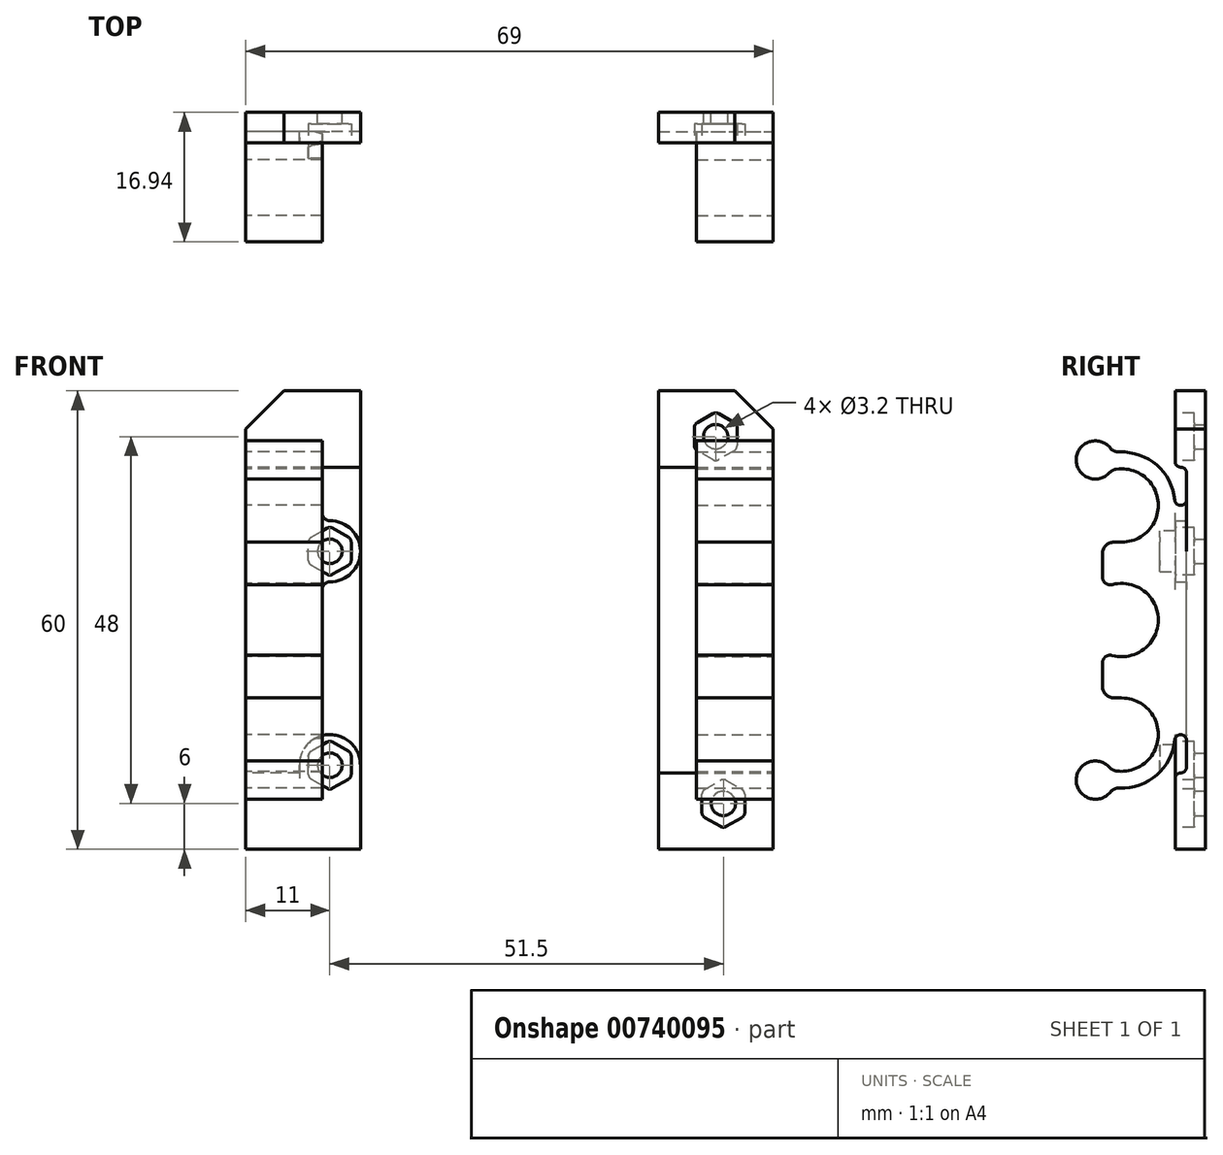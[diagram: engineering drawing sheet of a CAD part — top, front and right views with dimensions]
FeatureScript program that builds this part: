
annotation { "Feature Type Name" : "Feature", "Feature Type Description" : "" }
export const myFeature = defineFeature(function(context is Context, id is Id, definition is map)
    precondition{}
    {
        {
            var Q0;
            Q0=qCreatedBy(makeId("Right.planeOp"),FACE);
            var sketch = newSketch(context, id + "F0", { "sketchPlane" : qUnion([Q0])});
            skLineSegment(sketch, "E0.0", {"start": v(11, -45) * mm, "end": v(11, 15) * mm});
            skLineSegment(sketch, "E1.0", {"start": v(8.5, -34.25) * mm, "end": v(8.5, 4.25) * mm});
            skLineSegment(sketch, "E2.0", {"start": v(7, 5.75) * mm, "end": v(7, 15) * mm});
            skLineSegment(sketch, "E3.0", {"start": v(0, -37) * mm, "end": v(0, 7) * mm, "construction": true});
            skLineSegment(sketch, "E4", {"start": v(11, -15) * mm, "end": v(0, -15) * mm, "construction": true});
            skArc(sketch, "E5", {"start": v(0, -4.8) * mm, "mid": v(4.79, 0.35) * mm, "end": v(-0.7, 4.75) * mm});
            skCircle(sketch, "E6", {"center": v(0, 0) * mm, "radius": 4.38 * mm, "construction": true});
            skArc(sketch, "E7", {"start": v(6.97, 0.7) * mm, "mid": v(4.6, 5.28) * mm, "end": v(-0.29, 7) * mm});
            skLineSegment(sketch, "E8", {"start": v(0, 0) * mm, "end": v(-4.69, 8.12) * mm, "construction": true});
            skArc(sketch, "E9", {"start": v(-1.5, 7.54) * mm, "mid": v(-5.94, 6.02) * mm, "end": v(-1.59, 4.27) * mm});
            skLineSegment(sketch, "E10.0", {"start": v(-2.5, -23.7) * mm, "end": v(-2.5, -20.6) * mm});
            skLineSegment(sketch, "E11.0", {"start": v(11, 15) * mm, "end": v(7, 15) * mm});
            skLineSegment(sketch, "E12.0", {"start": v(7.75, 5) * mm, "end": v(7.75, 5) * mm});
            skLineSegment(sketch, "E13", {"start": v(0, -4.8) * mm, "end": v(-1, -4.8) * mm});
            skArc(sketch, "E14.filletArc", {"start": v(-0.7, 4.75) * mm, "mid": v(-1.18, 4.59) * mm, "end": v(-1.59, 4.27) * mm});
            skArc(sketch, "E15.filletArc", {"start": v(-1.5, 7.54) * mm, "mid": v(-0.96, 7.12) * mm, "end": v(-0.29, 7) * mm});
            skArc(sketch, "E16.filletArc", {"start": v(-1, -4.8) * mm, "mid": v(-2.06, -5.24) * mm, "end": v(-2.5, -6.3) * mm});
            skArc(sketch, "E17.filletArc", {"start": v(8.5, 4.25) * mm, "mid": v(8.28, 4.78) * mm, "end": v(7.75, 5) * mm});
            skArc(sketch, "E18.filletArc", {"start": v(7, 5.75) * mm, "mid": v(7.22, 5.22) * mm, "end": v(7.75, 5) * mm});
            skPoint(sketch, "E19", {"position": v(0, -15) * mm});
            skArc(sketch, "E20.MirrorCS", {"start": v(8.5, -34.25) * mm, "mid": v(8.28, -34.78) * mm, "end": v(7.75, -35) * mm});
            skArc(sketch, "E21.MirrorCS", {"start": v(7, -35.75) * mm, "mid": v(7.22, -35.22) * mm, "end": v(7.75, -35) * mm});
            skArc(sketch, "E22.MirrorCS", {"start": v(-1.5, -37.54) * mm, "mid": v(-0.96, -37.12) * mm, "end": v(-0.29, -37) * mm});
            skArc(sketch, "E23.MirrorCS", {"start": v(-1, -25.2) * mm, "mid": v(-2.06, -24.76) * mm, "end": v(-2.5, -23.7) * mm});
            skLineSegment(sketch, "E24.MirrorCS", {"start": v(0, -25.2) * mm, "end": v(-1, -25.2) * mm});
            skArc(sketch, "E25.MirrorCS", {"start": v(-0.7, -34.75) * mm, "mid": v(-1.18, -34.59) * mm, "end": v(-1.59, -34.27) * mm});
            skLineSegment(sketch, "E26.MirrorCS", {"start": v(7, -35.75) * mm, "end": v(7, -45) * mm});
            skCircle(sketch, "E27.MirrorC", {"center": v(0, -30) * mm, "radius": 4.38 * mm, "construction": true});
            skArc(sketch, "E28.MirrorCS", {"start": v(0, -25.2) * mm, "mid": v(4.79, -30.35) * mm, "end": v(-0.7, -34.75) * mm});
            skArc(sketch, "E29.MirrorCS", {"start": v(-1.5, -37.54) * mm, "mid": v(-5.94, -36.02) * mm, "end": v(-1.59, -34.27) * mm});
            skLineSegment(sketch, "E30.MirrorCS", {"start": v(11, -45) * mm, "end": v(7, -45) * mm});
            skLineSegment(sketch, "E31.MirrorCS", {"start": v(7.75, -35) * mm, "end": v(7.75, -35) * mm});
            skLineSegment(sketch, "E32.MirrorCS", {"start": v(0, -30) * mm, "end": v(-4.69, -38.12) * mm, "construction": true});
            skPoint(sketch, "E33.0", {"position": v(11, -41.5) * mm});
            skLineSegment(sketch, "E34", {"start": v(0, 0) * mm, "end": v(8.5, 0) * mm, "construction": true});
            skArc(sketch, "E35", {"start": v(6.97, 0.7) * mm, "mid": v(7.77, 0) * mm, "end": v(8.5, 0.77) * mm});
            skArc(sketch, "E36.MirrorCS", {"start": v(6.97, -30.7) * mm, "mid": v(7.77, -30) * mm, "end": v(8.5, -30.77) * mm});
            skArc(sketch, "E37.MirrorCS", {"start": v(6.97, -30.7) * mm, "mid": v(4.6, -35.28) * mm, "end": v(-0.29, -37) * mm});
            skArc(sketch, "E38", {"start": v(-1.24, -19.64) * mm, "mid": v(4.8, -15) * mm, "end": v(-1.24, -10.36) * mm});
            skLineSegment(sketch, "E39.trimOffspring", {"start": v(-2.5, -9.4) * mm, "end": v(-2.5, -6.3) * mm});
            skArc(sketch, "E40.filletArc", {"start": v(-2.5, -9.4) * mm, "mid": v(-2.1, -10.2) * mm, "end": v(-1.24, -10.36) * mm});
            skArc(sketch, "E41.filletArc", {"start": v(-1.24, -19.64) * mm, "mid": v(-2.1, -19.8) * mm, "end": v(-2.5, -20.6) * mm});
            skSolve(sketch);
        }
        {
            var Q0;
            Q0=makeQuery(id+"F0.imprint","IMPRINT",FACE,{"disambiguationData":[TD([[makeQuery(id+"F0.imprint","IMPRINT",EDGE,{"derivedFrom":sQuery(id+"F0.wireOp",EDGE,"E0.0")}),1.0]])]});
            extrude(context, id + "F1", {"entities" : qUnion([Q0]), "depth" : 15 * mm, "offsetDistance" : 25 * mm});
        }
        {
            var Q0;
            Q0=makeQuery(id+"F0.imprint","IMPRINT",FACE,{"disambiguationData":[TD([[makeQuery(id+"F0.imprint","IMPRINT",EDGE,{"derivedFrom":sQuery(id+"F0.wireOp",EDGE,"E5")}),-1.0]])]});
            extrude(context, id + "F2", {"entities" : qUnion([Q0]), "operationType" : NewBodyOperationType.ADD, "depth" : 10 * mm, "offsetDistance" : 25 * mm});
        }
        {
            var Q0;
            Q0=makeQuery(id+"F1.opExtrude","CAP_EDGE",EDGE,{"disambiguationData":[OSD([sQuery(id+"F0.wireOp",EDGE,"E11.0")])],"isStart":true});
            chamfer(context, id + "F3", {"entities" : qUnion([Q0]), "width" : 5 * mm, "tangentPropagation" : true});
        }
        {
            var Q0;
            Q0=makeQuery(id+"F1.opExtrude","SWEPT_BODY",BODY,{"disambiguationData":[OSD([sQuery(id+"F0.wireOp",EDGE,"E0.0"),sQuery(id+"F0.wireOp",EDGE,"E1.0"),sQuery(id+"F0.wireOp",EDGE,"E2.0"),sQuery(id+"F0.wireOp",EDGE,"E11.0"),sQuery(id+"F0.wireOp",EDGE,"E17.filletArc"),sQuery(id+"F0.wireOp",EDGE,"E18.filletArc"),sQuery(id+"F0.wireOp",EDGE,"E20.MirrorCS"),sQuery(id+"F0.wireOp",EDGE,"E21.MirrorCS"),sQuery(id+"F0.wireOp",EDGE,"E26.MirrorCS"),sQuery(id+"F0.wireOp",EDGE,"E30.MirrorCS")])]});
            var Q1;
            Q1=qCreatedBy(makeId("Right.planeOp"),FACE);
            mirror(context, id + "F4", {"entities" : qUnion([Q0]), "mirrorPlane" : qUnion([Q1])});
        }
        {
            var Q0;
            Q0=makeQuery(id+"F4.opPattern","COPY",BODY,{"derivedFrom":makeQuery(id+"F1.opExtrude","SWEPT_BODY",BODY,{"disambiguationData":[OSD([sQuery(id+"F0.wireOp",EDGE,"E0.0"),sQuery(id+"F0.wireOp",EDGE,"E1.0"),sQuery(id+"F0.wireOp",EDGE,"E2.0"),sQuery(id+"F0.wireOp",EDGE,"E11.0"),sQuery(id+"F0.wireOp",EDGE,"E17.filletArc"),sQuery(id+"F0.wireOp",EDGE,"E18.filletArc"),sQuery(id+"F0.wireOp",EDGE,"E20.MirrorCS"),sQuery(id+"F0.wireOp",EDGE,"E21.MirrorCS"),sQuery(id+"F0.wireOp",EDGE,"E26.MirrorCS"),sQuery(id+"F0.wireOp",EDGE,"E30.MirrorCS")])]}),"instanceName":"1"});
            transform(context, id + "F5", {"entities" : qUnion([Q0]), "transformType" : TransformType.TRANSLATION_3D, "dx" : 69 * mm, "dy" : 0 * mm, "dz" : 0 * mm, "makeCopy" : false});
        }
        {
            var Q0;
            Q0=makeQuery(id+"F1.opExtrude","SWEPT_FACE",FACE,{"disambiguationData":[OSD([sQuery(id+"F0.wireOp",EDGE,"E0.0")])]});
            var sketch = newSketch(context, id + "F6", { "sketchPlane" : qUnion([Q0])});
            skCircle(sketch, "E42", {"center": v(-11, -6) * mm, "radius": 1.6 * mm});
            skCircle(sketch, "E43", {"center": v(-11, -34) * mm, "radius": 1.6 * mm});
            skCircle(sketch, "E44", {"center": v(-61.5, 9) * mm, "radius": 1.6 * mm});
            skCircle(sketch, "E45", {"center": v(-62.5, -39) * mm, "radius": 1.6 * mm});
            skLineSegment(sketch, "E46.0", {"start": v(0, -45) * mm, "end": v(0, 10) * mm, "construction": true});
            skLineSegment(sketch, "E46.1", {"start": v(0, 10) * mm, "end": v(-5, 15) * mm, "construction": true});
            skLineSegment(sketch, "E46.2", {"start": v(-15, 15) * mm, "end": v(-5, 15) * mm, "construction": true});
            skLineSegment(sketch, "E46.3", {"start": v(-15, -45) * mm, "end": v(-15, 15) * mm, "construction": true});
            skLineSegment(sketch, "E46.4", {"start": v(-15, -45) * mm, "end": v(0, -45) * mm, "construction": true});
            skLineSegment(sketch, "E46.5", {"start": v(-54, 15) * mm, "end": v(-64, 15) * mm, "construction": true});
            skLineSegment(sketch, "E46.6", {"start": v(-69, 10) * mm, "end": v(-64, 15) * mm, "construction": true});
            skLineSegment(sketch, "E46.7", {"start": v(-69, -45) * mm, "end": v(-69, 10) * mm, "construction": true});
            skLineSegment(sketch, "E46.8", {"start": v(-54, -45) * mm, "end": v(-69, -45) * mm, "construction": true});
            skLineSegment(sketch, "E46.9", {"start": v(-54, -45) * mm, "end": v(-54, 15) * mm, "construction": true});
            skLineSegment(sketch, "E47", {"start": v(-11, -6) * mm, "end": v(-11, -34) * mm, "construction": true});
            skArc(sketch, "E48", {"start": v(-11, -2) * mm, "mid": v(-15, -6) * mm, "end": v(-11, -10) * mm});
            skArc(sketch, "E49", {"start": v(-7, -34) * mm, "mid": v(-11, -30) * mm, "end": v(-15, -34) * mm});
            skLineSegment(sketch, "E50.0", {"start": v(-15, -35.75) * mm, "end": v(-7, -35.75) * mm});
            skLineSegment(sketch, "E50.1", {"start": v(-10, -11) * mm, "end": v(-10, -1) * mm});
            skArc(sketch, "E51.filletArc", {"start": v(-10, -11) * mm, "mid": v(-10.3, -10.3) * mm, "end": v(-11, -10) * mm});
            skArc(sketch, "E52.filletArc", {"start": v(-11, -2) * mm, "mid": v(-10.3, -1.7) * mm, "end": v(-10, -1) * mm});
            skLineSegment(sketch, "E53", {"start": v(-7, -34) * mm, "end": v(-7, -35.75) * mm});
            skLineSegment(sketch, "E54", {"start": v(-15, -34) * mm, "end": v(-15, -35.75) * mm});
            skPoint(sketch, "E55.orphan", {"position": v(0, -35.75) * mm});
            skSolve(sketch);
        }
        {
            var Q0;
            {var subQ0=sQuery(id+"F6.wireOp",EDGE,"E51.filletArc");Q0=makeQuery(id+"F6.imprint","IMPRINT",FACE,{"disambiguationData":[TD([[makeQuery(id+"F6.imprint","IMPRINT",EDGE,{"derivedFrom":subQ0}),-1.0]])]});}
            var Q1;
            Q1=makeQuery(id+"F6.imprint","IMPRINT",FACE,{"disambiguationData":[TD([[makeQuery(id+"F6.imprint","IMPRINT",EDGE,{"derivedFrom":sQuery(id+"F6.wireOp",EDGE,"E43")}),-1.0]])]});
            extrude(context, id + "F7", {"entities" : qUnion([Q0, Q1]), "operationType" : NewBodyOperationType.ADD, "oppositeDirection" : true, "depth" : 4 * mm, "offsetDistance" : 25 * mm});
        }
        {
            var Q0;
            {var subQ0=sQuery(id+"F6.wireOp",EDGE,"E50.1");var subQ1=sQuery(id+"F6.wireOp",EDGE,"E42");var subQ2=makeQuery(id+"F6.imprint","INTERSECT",VERTEX,{"disambiguationData":[OD(0.0)],"derivedFrom":[subQ1,subQ0]});Q0=makeQuery(id+"F6.imprint","IMPRINT",FACE,{"disambiguationData":[TD([[makeQuery(id+"F6.imprint","IMPRINT",EDGE,{"disambiguationData":[TD([[subQ2,1.0]])],"derivedFrom":subQ1}),1.0]])]});}
            var Q1;
            {var subQ0=sQuery(id+"F6.wireOp",EDGE,"E50.1");var subQ1=sQuery(id+"F6.wireOp",EDGE,"E42");var subQ2=makeQuery(id+"F6.imprint","INTERSECT",VERTEX,{"disambiguationData":[OD(0.0)],"derivedFrom":[subQ1,subQ0]});Q1=makeQuery(id+"F6.imprint","IMPRINT",FACE,{"disambiguationData":[TD([[makeQuery(id+"F6.imprint","IMPRINT",EDGE,{"disambiguationData":[TD([[subQ2,-1.0]])],"derivedFrom":subQ1}),1.0]])]});}
            extrude(context, id + "F8", {"entities" : qUnion([Q0, Q1]), "operationType" : NewBodyOperationType.REMOVE, "oppositeDirection" : true, "depth" : 6 * mm, "offsetDistance" : 25 * mm});
        }
        {
            var Q0;
            Q0=makeQuery(id+"F6.imprint","IMPRINT",FACE,{"disambiguationData":[TD([[makeQuery(id+"F6.imprint","IMPRINT",EDGE,{"derivedFrom":sQuery(id+"F6.wireOp",EDGE,"E43")}),1.0]])]});
            var Q1;
            Q1=makeQuery(id+"F6.imprint","IMPRINT",FACE,{"disambiguationData":[TD([[makeQuery(id+"F6.imprint","IMPRINT",EDGE,{"derivedFrom":sQuery(id+"F6.wireOp",EDGE,"E44")}),1.0]])]});
            var Q2;
            Q2=makeQuery(id+"F6.imprint","IMPRINT",FACE,{"disambiguationData":[TD([[makeQuery(id+"F6.imprint","IMPRINT",EDGE,{"derivedFrom":sQuery(id+"F6.wireOp",EDGE,"E45")}),1.0]])]});
            extrude(context, id + "F9", {"entities" : qUnion([Q0, Q1, Q2]), "operationType" : NewBodyOperationType.REMOVE, "oppositeDirection" : true, "depth" : 4 * mm, "offsetDistance" : 25 * mm});
        }
        {
            var Q0;
            Q0=makeQuery(id+"F1.opExtrude","SWEPT_FACE",FACE,{"disambiguationData":[OSD([sQuery(id+"F0.wireOp",EDGE,"E2.0")])]});
            var sketch = newSketch(context, id + "F10", { "sketchPlane" : qUnion([Q0])});
            skCircle(sketch, "E56.cCircle", {"center": v(11, -6) * mm, "radius": 2.8 * mm, "construction": true});
            skLineSegment(sketch, "E56.0", {"start": v(13.8, -4.82) * mm, "end": v(13.8, -7.18) * mm});
            skLineSegment(sketch, "E56.1", {"start": v(13.43, -7.83) * mm, "end": v(11.38, -9.02) * mm});
            skLineSegment(sketch, "E56.2", {"start": v(10.62, -9.02) * mm, "end": v(8.58, -7.83) * mm});
            skLineSegment(sketch, "E56.3", {"start": v(8.2, -7.18) * mm, "end": v(8.2, -4.82) * mm});
            skLineSegment(sketch, "E56.4", {"start": v(8.57, -4.17) * mm, "end": v(10.62, -2.98) * mm});
            skLineSegment(sketch, "E56.5", {"start": v(11.38, -2.98) * mm, "end": v(13.43, -4.17) * mm});
            skPoint(sketch, "E56.0.midPoint", {"position": v(13.8, -6) * mm});
            skCircle(sketch, "E57.cCircle", {"center": v(11, -34) * mm, "radius": 2.8 * mm, "construction": true});
            skLineSegment(sketch, "E57.0", {"start": v(13.8, -32.82) * mm, "end": v(13.8, -35.18) * mm});
            skLineSegment(sketch, "E57.1", {"start": v(13.42, -35.83) * mm, "end": v(11.37, -37.02) * mm});
            skLineSegment(sketch, "E57.2", {"start": v(10.62, -37.02) * mm, "end": v(8.57, -35.83) * mm});
            skLineSegment(sketch, "E57.3", {"start": v(8.2, -35.18) * mm, "end": v(8.2, -32.82) * mm});
            skLineSegment(sketch, "E57.4", {"start": v(8.57, -32.17) * mm, "end": v(10.62, -30.98) * mm});
            skLineSegment(sketch, "E57.5", {"start": v(11.37, -30.98) * mm, "end": v(13.43, -32.17) * mm});
            skPoint(sketch, "E57.0.midPoint", {"position": v(13.8, -34) * mm});
            skCircle(sketch, "E58.cCircle", {"center": v(61.5, 9) * mm, "radius": 2.8 * mm, "construction": true});
            skLineSegment(sketch, "E58.0", {"start": v(64.3, 10.18) * mm, "end": v(64.3, 7.82) * mm});
            skLineSegment(sketch, "E58.1", {"start": v(63.92, 7.17) * mm, "end": v(61.88, 5.98) * mm});
            skLineSegment(sketch, "E58.2", {"start": v(61.12, 5.98) * mm, "end": v(59.08, 7.17) * mm});
            skLineSegment(sketch, "E58.3", {"start": v(58.7, 7.82) * mm, "end": v(58.7, 10.18) * mm});
            skLineSegment(sketch, "E58.4", {"start": v(59.08, 10.83) * mm, "end": v(61.13, 12.02) * mm});
            skLineSegment(sketch, "E58.5", {"start": v(61.88, 12.02) * mm, "end": v(63.92, 10.83) * mm});
            skPoint(sketch, "E58.0.midPoint", {"position": v(64.3, 9) * mm});
            skCircle(sketch, "E59.cCircle", {"center": v(62.5, -39) * mm, "radius": 2.8 * mm, "construction": true});
            skLineSegment(sketch, "E59.0", {"start": v(65.3, -37.82) * mm, "end": v(65.3, -40.18) * mm});
            skLineSegment(sketch, "E59.1", {"start": v(64.92, -40.83) * mm, "end": v(62.88, -42.02) * mm});
            skLineSegment(sketch, "E59.2", {"start": v(62.13, -42.02) * mm, "end": v(60.07, -40.83) * mm});
            skLineSegment(sketch, "E59.3", {"start": v(59.7, -40.18) * mm, "end": v(59.7, -37.82) * mm});
            skLineSegment(sketch, "E59.4", {"start": v(60.07, -37.17) * mm, "end": v(62.12, -35.98) * mm});
            skLineSegment(sketch, "E59.5", {"start": v(62.88, -35.98) * mm, "end": v(64.92, -37.17) * mm});
            skPoint(sketch, "E59.0.midPoint", {"position": v(65.3, -39) * mm});
            skPoint(sketch, "E60.visualSharp", {"position": v(13.8, -4.38) * mm});
            skArc(sketch, "E60.filletArc", {"start": v(13.8, -4.82) * mm, "mid": v(13.7, -4.44) * mm, "end": v(13.43, -4.17) * mm});
            skPoint(sketch, "E61.visualSharp", {"position": v(11, -2.77) * mm});
            skArc(sketch, "E61.filletArc", {"start": v(11.38, -2.98) * mm, "mid": v(11, -2.88) * mm, "end": v(10.62, -2.98) * mm});
            skPoint(sketch, "E62.visualSharp", {"position": v(8.2, -4.38) * mm});
            skArc(sketch, "E62.filletArc", {"start": v(8.57, -4.17) * mm, "mid": v(8.3, -4.44) * mm, "end": v(8.2, -4.82) * mm});
            skPoint(sketch, "E63.visualSharp", {"position": v(8.2, -7.62) * mm});
            skArc(sketch, "E63.filletArc", {"start": v(8.2, -7.18) * mm, "mid": v(8.3, -7.56) * mm, "end": v(8.58, -7.83) * mm});
            skPoint(sketch, "E64.visualSharp", {"position": v(11, -9.23) * mm});
            skArc(sketch, "E64.filletArc", {"start": v(10.62, -9.02) * mm, "mid": v(11, -9.12) * mm, "end": v(11.38, -9.02) * mm});
            skPoint(sketch, "E65.visualSharp", {"position": v(13.8, -7.62) * mm});
            skArc(sketch, "E65.filletArc", {"start": v(13.43, -7.83) * mm, "mid": v(13.7, -7.56) * mm, "end": v(13.8, -7.18) * mm});
            skPoint(sketch, "E66.visualSharp", {"position": v(13.8, -32.38) * mm});
            skArc(sketch, "E66.filletArc", {"start": v(13.8, -32.82) * mm, "mid": v(13.7, -32.44) * mm, "end": v(13.42, -32.17) * mm});
            skPoint(sketch, "E67.visualSharp", {"position": v(11, -30.77) * mm});
            skArc(sketch, "E67.filletArc", {"start": v(11.37, -30.98) * mm, "mid": v(11, -30.88) * mm, "end": v(10.62, -30.98) * mm});
            skPoint(sketch, "E68.visualSharp", {"position": v(8.2, -32.38) * mm});
            skArc(sketch, "E68.filletArc", {"start": v(8.57, -32.17) * mm, "mid": v(8.3, -32.44) * mm, "end": v(8.2, -32.82) * mm});
            skPoint(sketch, "E69.visualSharp", {"position": v(8.2, -35.62) * mm});
            skArc(sketch, "E69.filletArc", {"start": v(8.2, -35.18) * mm, "mid": v(8.3, -35.56) * mm, "end": v(8.57, -35.83) * mm});
            skPoint(sketch, "E70.visualSharp", {"position": v(11, -37.23) * mm});
            skArc(sketch, "E70.filletArc", {"start": v(10.62, -37.02) * mm, "mid": v(11, -37.12) * mm, "end": v(11.38, -37.02) * mm});
            skPoint(sketch, "E71.visualSharp", {"position": v(13.8, -35.62) * mm});
            skArc(sketch, "E71.filletArc", {"start": v(13.42, -35.83) * mm, "mid": v(13.7, -35.56) * mm, "end": v(13.8, -35.18) * mm});
            skPoint(sketch, "E72.visualSharp", {"position": v(64.3, 10.62) * mm});
            skArc(sketch, "E72.filletArc", {"start": v(64.3, 10.18) * mm, "mid": v(64.2, 10.56) * mm, "end": v(63.92, 10.83) * mm});
            skPoint(sketch, "E73.visualSharp", {"position": v(61.5, 12.23) * mm});
            skArc(sketch, "E73.filletArc", {"start": v(61.88, 12.02) * mm, "mid": v(61.5, 12.12) * mm, "end": v(61.12, 12.02) * mm});
            skPoint(sketch, "E74.visualSharp", {"position": v(58.7, 10.62) * mm});
            skArc(sketch, "E74.filletArc", {"start": v(59.08, 10.83) * mm, "mid": v(58.8, 10.56) * mm, "end": v(58.7, 10.18) * mm});
            skPoint(sketch, "E75.visualSharp", {"position": v(58.7, 7.38) * mm});
            skArc(sketch, "E75.filletArc", {"start": v(58.7, 7.82) * mm, "mid": v(58.8, 7.44) * mm, "end": v(59.08, 7.17) * mm});
            skPoint(sketch, "E76.visualSharp", {"position": v(61.5, 5.77) * mm});
            skArc(sketch, "E76.filletArc", {"start": v(61.12, 5.98) * mm, "mid": v(61.5, 5.88) * mm, "end": v(61.88, 5.98) * mm});
            skPoint(sketch, "E77.visualSharp", {"position": v(64.3, 7.38) * mm});
            skArc(sketch, "E77.filletArc", {"start": v(63.92, 7.17) * mm, "mid": v(64.2, 7.44) * mm, "end": v(64.3, 7.82) * mm});
            skPoint(sketch, "E78.visualSharp", {"position": v(65.3, -37.38) * mm});
            skArc(sketch, "E78.filletArc", {"start": v(65.3, -37.82) * mm, "mid": v(65.2, -37.44) * mm, "end": v(64.92, -37.17) * mm});
            skPoint(sketch, "E79.visualSharp", {"position": v(62.5, -35.77) * mm});
            skArc(sketch, "E79.filletArc", {"start": v(62.88, -35.98) * mm, "mid": v(62.5, -35.88) * mm, "end": v(62.13, -35.98) * mm});
            skPoint(sketch, "E80.visualSharp", {"position": v(59.7, -37.38) * mm});
            skArc(sketch, "E80.filletArc", {"start": v(60.07, -37.17) * mm, "mid": v(59.8, -37.44) * mm, "end": v(59.7, -37.82) * mm});
            skPoint(sketch, "E81.visualSharp", {"position": v(59.7, -40.62) * mm});
            skArc(sketch, "E81.filletArc", {"start": v(59.7, -40.18) * mm, "mid": v(59.8, -40.56) * mm, "end": v(60.07, -40.83) * mm});
            skPoint(sketch, "E82.visualSharp", {"position": v(62.5, -42.23) * mm});
            skArc(sketch, "E82.filletArc", {"start": v(62.13, -42.02) * mm, "mid": v(62.5, -42.12) * mm, "end": v(62.88, -42.02) * mm});
            skPoint(sketch, "E83.visualSharp", {"position": v(65.3, -40.62) * mm});
            skArc(sketch, "E83.filletArc", {"start": v(64.92, -40.83) * mm, "mid": v(65.2, -40.56) * mm, "end": v(65.3, -40.18) * mm});
            skSolve(sketch);
        }
        {
            var Q0;
            Q0 = qSketchRegion(id + "F10", true);
            extrude(context, id + "F11", {"entities" : qUnion([Q0]), "operationType" : NewBodyOperationType.REMOVE, "oppositeDirection" : true, "depth" : 2.5 * mm, "offsetDistance" : 25 * mm});
        }
        {
            var Q0;
            Q0=makeQuery(id+"F10.imprint","IMPRINT",FACE,{"disambiguationData":[TD([[makeQuery(id+"F10.imprint","IMPRINT",EDGE,{"derivedFrom":sQuery(id+"F10.wireOp",EDGE,"E56.0")}),-1.0]])]});
            var Q1;
            Q1=makeQuery(id+"F10.imprint","IMPRINT",FACE,{"disambiguationData":[TD([[makeQuery(id+"F10.imprint","IMPRINT",EDGE,{"derivedFrom":sQuery(id+"F10.wireOp",EDGE,"E57.0")}),-1.0]])]});
            extrude(context, id + "F12", {"entities" : qUnion([Q0, Q1]), "operationType" : NewBodyOperationType.REMOVE, "depth" : 2 * mm, "offsetDistance" : 25 * mm});
        }
    });
